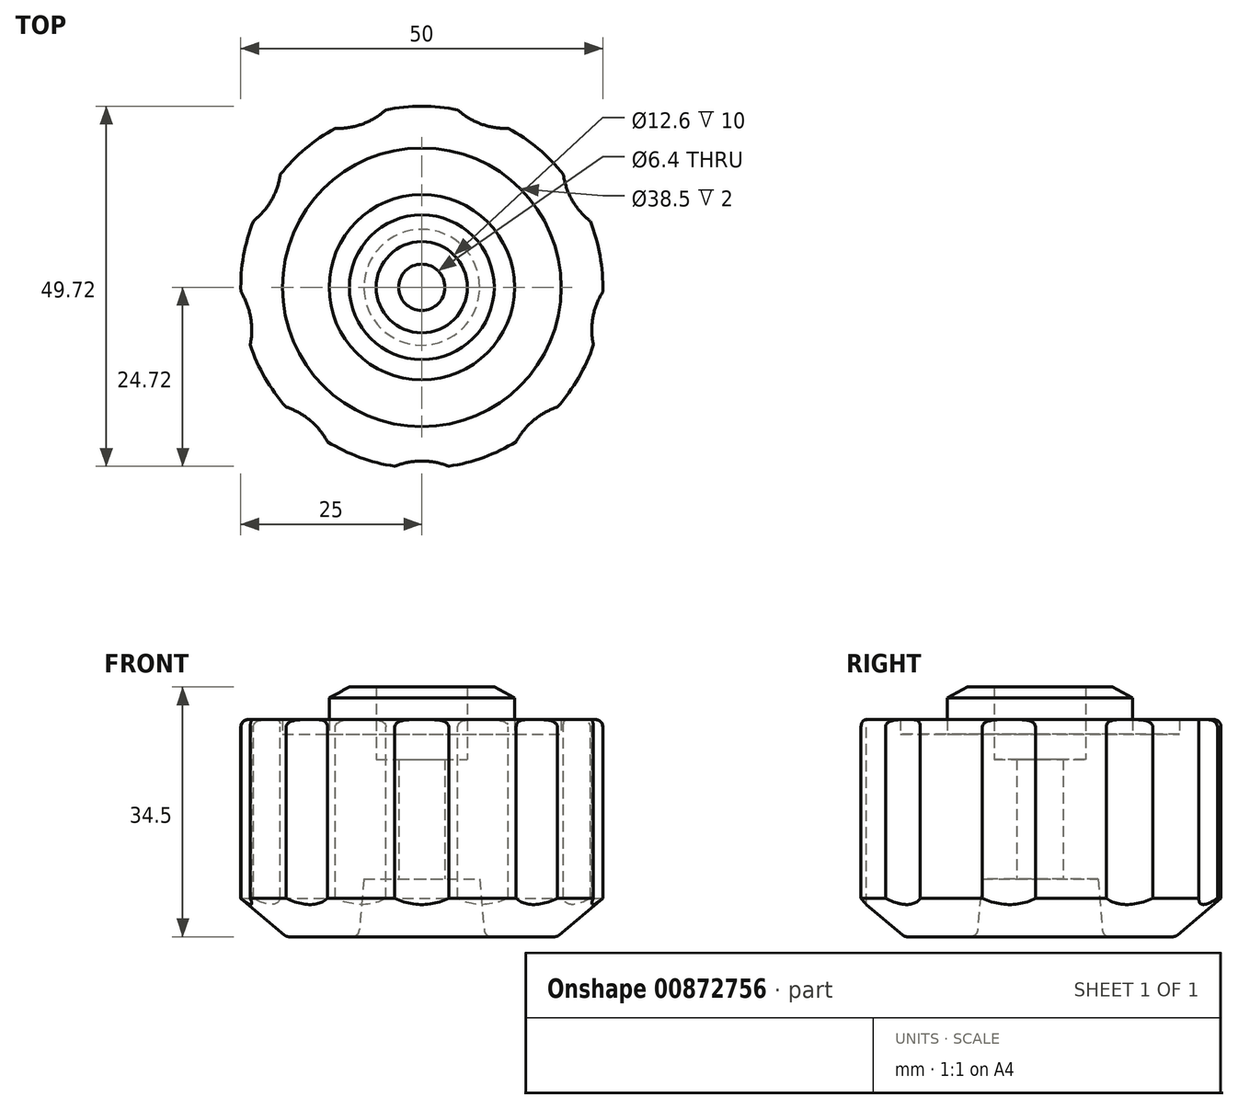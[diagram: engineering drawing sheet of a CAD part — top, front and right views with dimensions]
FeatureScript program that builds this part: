
annotation { "Feature Type Name" : "Feature", "Feature Type Description" : "" }
export const myFeature = defineFeature(function(context is Context, id is Id, definition is map)
    precondition{}
    {
        {
            var Q0;
            Q0=qCreatedBy(makeId("Front.planeOp"),FACE);
            var sketch = newSketch(context, id + "F0", { "sketchPlane" : qUnion([Q0])});
            skLineSegment(sketch, "E0", {"start": v(0, -6.14) * mm, "end": v(0, 36.57) * mm, "construction": true});
            skLineSegment(sketch, "E1", {"start": v(8.7, 0) * mm, "end": v(18.7, 0) * mm});
            skLineSegment(sketch, "E2", {"start": v(18.7, 0) * mm, "end": v(25, 5.29) * mm});
            skLineSegment(sketch, "E3", {"start": v(25, 5.29) * mm, "end": v(25, 30) * mm});
            skLineSegment(sketch, "E4", {"start": v(25, 30) * mm, "end": v(19.25, 30) * mm});
            skLineSegment(sketch, "E5", {"start": v(19.25, 30) * mm, "end": v(19.25, 28) * mm});
            skLineSegment(sketch, "E6", {"start": v(6.3, 34.5) * mm, "end": v(6.3, 24.5) * mm});
            skLineSegment(sketch, "E7", {"start": v(6.3, 24.5) * mm, "end": v(3.2, 24.5) * mm});
            skLineSegment(sketch, "E8", {"start": v(3.2, 24.5) * mm, "end": v(3.2, 8) * mm});
            skLineSegment(sketch, "E9", {"start": v(3.2, 8) * mm, "end": v(8, 8) * mm});
            skLineSegment(sketch, "E10", {"start": v(8, 8) * mm, "end": v(8.7, 0) * mm});
            skLineSegment(sketch, "E11", {"start": v(-29.63, 0) * mm, "end": v(44.02, 0) * mm, "construction": true});
            skLineSegment(sketch, "E12", {"start": v(19.25, 28) * mm, "end": v(12.8, 28) * mm});
            skLineSegment(sketch, "E13", {"start": v(10, 34.5) * mm, "end": v(6.3, 34.5) * mm});
            skLineSegment(sketch, "E14", {"start": v(12.8, 28) * mm, "end": v(12.8, 33) * mm});
            skLineSegment(sketch, "E15", {"start": v(12.8, 33) * mm, "end": v(10, 34.5) * mm});
            skSolve(sketch);
        }
        {
            var Q0;
            Q0=makeQuery(id+"F0.imprint","IMPRINT",FACE,{"disambiguationData":[TD([[makeQuery(id+"F0.imprint","IMPRINT",EDGE,{"derivedFrom":sQuery(id+"F0.wireOp",EDGE,"E1")}),1.0]])]});
            var Q1;
            Q1=sQuery(id+"F0.wireOp",EDGE,"E0");
            revolve(context, id + "F1", {"surfaceOperationType" : NewSurfaceOperationType.NEW, "entities" : qUnion([Q0]), "axis" : qUnion([Q1]), "revolveType" : RevolveType.FULL});
        }
        {
            var Q0;
            Q0=makeQuery(id+"F1.opRevolve","SWEPT_FACE",FACE,{"disambiguationData":[OSD([sQuery(id+"F0.wireOp",EDGE,"E4")])]});
            var sketch = newSketch(context, id + "F2", { "sketchPlane" : qUnion([Q0])});
            skLineSegment(sketch, "E16", {"start": v(0, 0) * mm, "end": v(0, 71.94) * mm, "construction": true});
            skLineSegment(sketch, "E17", {"start": v(0, 0) * mm, "end": v(26.2, 71.99) * mm, "construction": true});
            skCircle(sketch, "E18", {"center": v(11.63, 31.95) * mm, "radius": 10 * mm});
            skCircle(sketch, "E19.1.0", {"center": v(-11.63, 31.95) * mm, "radius": 10 * mm});
            skCircle(sketch, "E19.2.0", {"center": v(-29.44, 17) * mm, "radius": 10 * mm});
            skCircle(sketch, "E19.3.0", {"center": v(-33.48, -5.9) * mm, "radius": 10 * mm});
            skCircle(sketch, "E19.4.0", {"center": v(-21.85, -26.05) * mm, "radius": 10 * mm});
            skCircle(sketch, "E19.5.0", {"center": v(0, -34) * mm, "radius": 10 * mm});
            skCircle(sketch, "E19.6.0", {"center": v(21.85, -26.05) * mm, "radius": 10 * mm});
            skCircle(sketch, "E19.7.0", {"center": v(33.48, -5.9) * mm, "radius": 10 * mm});
            skCircle(sketch, "E19.8.0", {"center": v(29.44, 17) * mm, "radius": 10 * mm});
            skPoint(sketch, "E19.center", {"position": v(0, 0) * mm});
            skSolve(sketch);
        }
        {
            var Q0;
            Q0 = qSketchRegion(id + "F2", true);
            extrude(context, id + "F3", {"entities" : qUnion([Q0]), "operationType" : NewBodyOperationType.REMOVE, "endBound" : BoundingType.THROUGH_ALL, "oppositeDirection" : true, "depth" : 25 * mm, "offsetDistance" : 25 * mm});
        }
        {
            var Q0;
            Q0=makeQuery(id+"F1.opRevolve","SWEPT_EDGE",EDGE,{"disambiguationData":[OSD([sQuery(id+"F0.wireOp",EDGE,"E1"),sQuery(id+"F0.wireOp",EDGE,"E10")])]});
            var Q1;
            Q1=makeQuery(id+"F1.opRevolve","SWEPT_EDGE",EDGE,{"disambiguationData":[OSD([sQuery(id+"F0.wireOp",EDGE,"E1"),sQuery(id+"F0.wireOp",EDGE,"E2")])]});
            fillet(context, id + "F4", {"entities" : qUnion([Q0, Q1]), "tangentPropagation" : true, "radius" : 1 * mm, "defaultsChanged" : true, "vertexSettings" : [], "allowEdgeOverflow" : false});
        }
        {
            var Q0;
            Q0=makeQuery(id+"F3.boolean.opBoolean","COPY",EDGE,{"derivedFrom":makeQuery(id+"F3.opExtrude","CAP_EDGE",EDGE,{"disambiguationData":[OSD([sQuery(id+"F2.wireOp",EDGE,"E19.4.0")])],"isStart":true})});
            var Q1;
            {var subQ0=sQuery(id+"F0.wireOp",EDGE,"E3");var subQ1=sQuery(id+"F0.wireOp",EDGE,"E4");Q1=makeQuery(id+"F3.boolean.opBoolean","SPLIT",EDGE,{"disambiguationData":[TD([makeQuery(id+"F1.opRevolve","SWEPT_FACE",FACE,{"disambiguationData":[OSD([subQ0])]}),makeQuery(id+"F1.opRevolve","SWEPT_FACE",FACE,{"disambiguationData":[OSD([subQ1])]}),makeQuery(id+"F3.opExtrude","SWEPT_FACE",FACE,{"disambiguationData":[OSD([sQuery(id+"F2.wireOp",EDGE,"E19.4.0")])]}),makeQuery(id+"F3.opExtrude","SWEPT_FACE",FACE,{"disambiguationData":[OSD([sQuery(id+"F2.wireOp",EDGE,"E19.5.0")])]})])],"derivedFrom":makeQuery(id+"F1.opRevolve","SWEPT_EDGE",EDGE,{"disambiguationData":[OSD([subQ0,subQ1])]})});}
            var Q2;
            {var subQ0=sQuery(id+"F0.wireOp",EDGE,"E3");var subQ1=sQuery(id+"F0.wireOp",EDGE,"E4");Q2=makeQuery(id+"F3.boolean.opBoolean","SPLIT",EDGE,{"disambiguationData":[TD([makeQuery(id+"F1.opRevolve","SWEPT_FACE",FACE,{"disambiguationData":[OSD([subQ0])]}),makeQuery(id+"F1.opRevolve","SWEPT_FACE",FACE,{"disambiguationData":[OSD([subQ1])]}),makeQuery(id+"F3.opExtrude","SWEPT_FACE",FACE,{"disambiguationData":[OSD([sQuery(id+"F2.wireOp",EDGE,"E19.3.0")])]}),makeQuery(id+"F3.opExtrude","SWEPT_FACE",FACE,{"disambiguationData":[OSD([sQuery(id+"F2.wireOp",EDGE,"E19.4.0")])]})])],"derivedFrom":makeQuery(id+"F1.opRevolve","SWEPT_EDGE",EDGE,{"disambiguationData":[OSD([subQ0,subQ1])]})});}
            var Q3;
            Q3=makeQuery(id+"F3.boolean.opBoolean","COPY",EDGE,{"derivedFrom":makeQuery(id+"F3.opExtrude","CAP_EDGE",EDGE,{"disambiguationData":[OSD([sQuery(id+"F2.wireOp",EDGE,"E19.3.0")])],"isStart":true})});
            var Q4;
            {var subQ0=sQuery(id+"F0.wireOp",EDGE,"E3");var subQ1=sQuery(id+"F0.wireOp",EDGE,"E4");Q4=makeQuery(id+"F3.boolean.opBoolean","SPLIT",EDGE,{"disambiguationData":[TD([makeQuery(id+"F1.opRevolve","SWEPT_FACE",FACE,{"disambiguationData":[OSD([subQ0])]}),makeQuery(id+"F1.opRevolve","SWEPT_FACE",FACE,{"disambiguationData":[OSD([subQ1])]}),makeQuery(id+"F3.opExtrude","SWEPT_FACE",FACE,{"disambiguationData":[OSD([sQuery(id+"F2.wireOp",EDGE,"E19.2.0")])]}),makeQuery(id+"F3.opExtrude","SWEPT_FACE",FACE,{"disambiguationData":[OSD([sQuery(id+"F2.wireOp",EDGE,"E19.3.0")])]})])],"derivedFrom":makeQuery(id+"F1.opRevolve","SWEPT_EDGE",EDGE,{"disambiguationData":[OSD([subQ0,subQ1])]})});}
            var Q5;
            Q5=makeQuery(id+"F3.boolean.opBoolean","COPY",EDGE,{"derivedFrom":makeQuery(id+"F3.opExtrude","CAP_EDGE",EDGE,{"disambiguationData":[OSD([sQuery(id+"F2.wireOp",EDGE,"E19.2.0")])],"isStart":true})});
            var Q6;
            {var subQ0=sQuery(id+"F0.wireOp",EDGE,"E3");var subQ1=sQuery(id+"F0.wireOp",EDGE,"E4");Q6=makeQuery(id+"F3.boolean.opBoolean","SPLIT",EDGE,{"disambiguationData":[TD([makeQuery(id+"F1.opRevolve","SWEPT_FACE",FACE,{"disambiguationData":[OSD([subQ0])]}),makeQuery(id+"F1.opRevolve","SWEPT_FACE",FACE,{"disambiguationData":[OSD([subQ1])]}),makeQuery(id+"F3.opExtrude","SWEPT_FACE",FACE,{"disambiguationData":[OSD([sQuery(id+"F2.wireOp",EDGE,"E19.1.0")])]}),makeQuery(id+"F3.opExtrude","SWEPT_FACE",FACE,{"disambiguationData":[OSD([sQuery(id+"F2.wireOp",EDGE,"E19.2.0")])]})])],"derivedFrom":makeQuery(id+"F1.opRevolve","SWEPT_EDGE",EDGE,{"disambiguationData":[OSD([subQ0,subQ1])]})});}
            var Q7;
            Q7=makeQuery(id+"F3.boolean.opBoolean","COPY",EDGE,{"derivedFrom":makeQuery(id+"F3.opExtrude","CAP_EDGE",EDGE,{"disambiguationData":[OSD([sQuery(id+"F2.wireOp",EDGE,"E19.1.0")])],"isStart":true})});
            var Q8;
            {var subQ0=sQuery(id+"F0.wireOp",EDGE,"E3");var subQ1=sQuery(id+"F0.wireOp",EDGE,"E4");Q8=makeQuery(id+"F3.boolean.opBoolean","SPLIT",EDGE,{"disambiguationData":[TD([makeQuery(id+"F1.opRevolve","SWEPT_FACE",FACE,{"disambiguationData":[OSD([subQ0])]}),makeQuery(id+"F1.opRevolve","SWEPT_FACE",FACE,{"disambiguationData":[OSD([subQ1])]}),makeQuery(id+"F3.opExtrude","SWEPT_FACE",FACE,{"disambiguationData":[OSD([sQuery(id+"F2.wireOp",EDGE,"E18")])]}),makeQuery(id+"F3.opExtrude","SWEPT_FACE",FACE,{"disambiguationData":[OSD([sQuery(id+"F2.wireOp",EDGE,"E19.1.0")])]})])],"derivedFrom":makeQuery(id+"F1.opRevolve","SWEPT_EDGE",EDGE,{"disambiguationData":[OSD([subQ0,subQ1])]})});}
            var Q9;
            Q9=makeQuery(id+"F3.boolean.opBoolean","COPY",EDGE,{"derivedFrom":makeQuery(id+"F3.opExtrude","CAP_EDGE",EDGE,{"disambiguationData":[OSD([sQuery(id+"F2.wireOp",EDGE,"E18")])],"isStart":true})});
            var Q10;
            {var subQ0=sQuery(id+"F0.wireOp",EDGE,"E3");var subQ1=sQuery(id+"F0.wireOp",EDGE,"E4");Q10=makeQuery(id+"F3.boolean.opBoolean","SPLIT",EDGE,{"disambiguationData":[TD([makeQuery(id+"F1.opRevolve","SWEPT_FACE",FACE,{"disambiguationData":[OSD([subQ0])]}),makeQuery(id+"F1.opRevolve","SWEPT_FACE",FACE,{"disambiguationData":[OSD([subQ1])]}),makeQuery(id+"F3.opExtrude","SWEPT_FACE",FACE,{"disambiguationData":[OSD([sQuery(id+"F2.wireOp",EDGE,"E18")])]}),makeQuery(id+"F3.opExtrude","SWEPT_FACE",FACE,{"disambiguationData":[OSD([sQuery(id+"F2.wireOp",EDGE,"E19.8.0")])]})])],"derivedFrom":makeQuery(id+"F1.opRevolve","SWEPT_EDGE",EDGE,{"disambiguationData":[OSD([subQ0,subQ1])]})});}
            var Q11;
            Q11=makeQuery(id+"F3.boolean.opBoolean","COPY",EDGE,{"derivedFrom":makeQuery(id+"F3.opExtrude","CAP_EDGE",EDGE,{"disambiguationData":[OSD([sQuery(id+"F2.wireOp",EDGE,"E19.8.0")])],"isStart":true})});
            var Q12;
            {var subQ0=sQuery(id+"F0.wireOp",EDGE,"E3");var subQ1=sQuery(id+"F0.wireOp",EDGE,"E4");Q12=makeQuery(id+"F3.boolean.opBoolean","SPLIT",EDGE,{"disambiguationData":[TD([makeQuery(id+"F1.opRevolve","SWEPT_FACE",FACE,{"disambiguationData":[OSD([subQ0])]}),makeQuery(id+"F1.opRevolve","SWEPT_FACE",FACE,{"disambiguationData":[OSD([subQ1])]}),makeQuery(id+"F3.opExtrude","SWEPT_FACE",FACE,{"disambiguationData":[OSD([sQuery(id+"F2.wireOp",EDGE,"E19.7.0")])]}),makeQuery(id+"F3.opExtrude","SWEPT_FACE",FACE,{"disambiguationData":[OSD([sQuery(id+"F2.wireOp",EDGE,"E19.8.0")])]})])],"derivedFrom":makeQuery(id+"F1.opRevolve","SWEPT_EDGE",EDGE,{"disambiguationData":[OSD([subQ0,subQ1])]})});}
            var Q13;
            Q13=makeQuery(id+"F3.boolean.opBoolean","COPY",EDGE,{"derivedFrom":makeQuery(id+"F3.opExtrude","CAP_EDGE",EDGE,{"disambiguationData":[OSD([sQuery(id+"F2.wireOp",EDGE,"E19.7.0")])],"isStart":true})});
            var Q14;
            {var subQ0=sQuery(id+"F0.wireOp",EDGE,"E3");var subQ1=sQuery(id+"F0.wireOp",EDGE,"E4");Q14=makeQuery(id+"F3.boolean.opBoolean","SPLIT",EDGE,{"disambiguationData":[TD([makeQuery(id+"F1.opRevolve","SWEPT_FACE",FACE,{"disambiguationData":[OSD([subQ0])]}),makeQuery(id+"F1.opRevolve","SWEPT_FACE",FACE,{"disambiguationData":[OSD([subQ1])]}),makeQuery(id+"F3.opExtrude","SWEPT_FACE",FACE,{"disambiguationData":[OSD([sQuery(id+"F2.wireOp",EDGE,"E19.6.0")])]}),makeQuery(id+"F3.opExtrude","SWEPT_FACE",FACE,{"disambiguationData":[OSD([sQuery(id+"F2.wireOp",EDGE,"E19.7.0")])]})])],"derivedFrom":makeQuery(id+"F1.opRevolve","SWEPT_EDGE",EDGE,{"disambiguationData":[OSD([subQ0,subQ1])]})});}
            var Q15;
            Q15=makeQuery(id+"F3.boolean.opBoolean","COPY",EDGE,{"derivedFrom":makeQuery(id+"F3.opExtrude","CAP_EDGE",EDGE,{"disambiguationData":[OSD([sQuery(id+"F2.wireOp",EDGE,"E19.6.0")])],"isStart":true})});
            var Q16;
            {var subQ0=sQuery(id+"F0.wireOp",EDGE,"E3");var subQ1=sQuery(id+"F0.wireOp",EDGE,"E4");Q16=makeQuery(id+"F3.boolean.opBoolean","SPLIT",EDGE,{"disambiguationData":[TD([makeQuery(id+"F1.opRevolve","SWEPT_FACE",FACE,{"disambiguationData":[OSD([subQ0])]}),makeQuery(id+"F1.opRevolve","SWEPT_FACE",FACE,{"disambiguationData":[OSD([subQ1])]}),makeQuery(id+"F3.opExtrude","SWEPT_FACE",FACE,{"disambiguationData":[OSD([sQuery(id+"F2.wireOp",EDGE,"E19.5.0")])]}),makeQuery(id+"F3.opExtrude","SWEPT_FACE",FACE,{"disambiguationData":[OSD([sQuery(id+"F2.wireOp",EDGE,"E19.6.0")])]})])],"derivedFrom":makeQuery(id+"F1.opRevolve","SWEPT_EDGE",EDGE,{"disambiguationData":[OSD([subQ0,subQ1])]})});}
            var Q17;
            Q17=makeQuery(id+"F3.boolean.opBoolean","COPY",EDGE,{"derivedFrom":makeQuery(id+"F3.opExtrude","CAP_EDGE",EDGE,{"disambiguationData":[OSD([sQuery(id+"F2.wireOp",EDGE,"E19.5.0")])],"isStart":true})});
            fillet(context, id + "F5", {"entities" : qUnion([Q0, Q1, Q2, Q3, Q4, Q5, Q6, Q7, Q8, Q9, Q10, Q11, Q12, Q13, Q14, Q15, Q16, Q17]), "tangentPropagation" : true, "radius" : 1 * mm, "defaultsChanged" : false, "vertexSettings" : [], "allowEdgeOverflow" : false});
        }
    });
